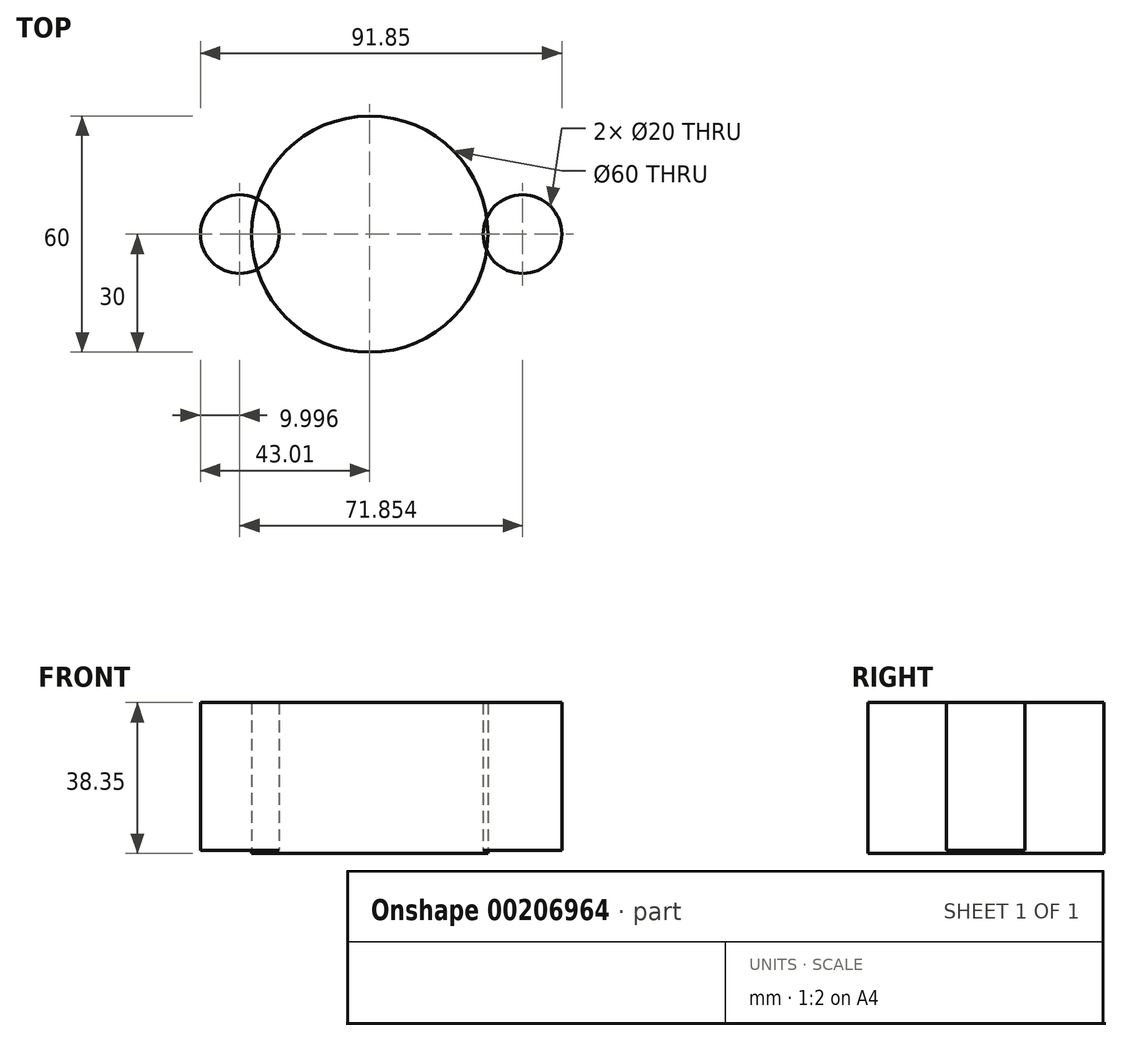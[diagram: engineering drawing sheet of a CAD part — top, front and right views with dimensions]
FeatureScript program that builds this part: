
annotation { "Feature Type Name" : "Feature", "Feature Type Description" : "" }
export const myFeature = defineFeature(function(context is Context, id is Id, definition is map)
    precondition{}
    {
        {
            var Q0;
            Q0=qCreatedBy(makeId("Top.planeOp"),FACE);
            var sketch = newSketch(context, id + "F0", { "sketchPlane" : qUnion([Q0])});
            skCircle(sketch, "E0", {"center": v(38.84, 0) * mm, "radius": 10 * mm});
            skCircle(sketch, "E1", {"center": v(-33.01, 0) * mm, "radius": 10 * mm});
            skCircle(sketch, "E2", {"center": v(0, 0) * mm, "radius": 30 * mm});
            skSolve(sketch);
        }
        {
            var Q0;
            Q0=sQuery(id+"F0.wireOp",EDGE,"E1");
            var Q1;
            Q1=sQuery(id+"F0.wireOp",EDGE,"E0");
            extrude(context, id + "F1", {"bodyType" : ToolBodyType.SURFACE, "surfaceEntities" : qUnion([Q0, Q1]), "oppositeDirection" : true, "depth" : 37.6 * mm});
        }
        {
            var Q0;
            Q0=sQuery(id+"F0.wireOp",EDGE,"E2");
            extrude(context, id + "F2", {"bodyType" : ToolBodyType.SURFACE, "surfaceEntities" : qUnion([Q0]), "oppositeDirection" : true, "depth" : 38.35 * mm});
        }
    });
